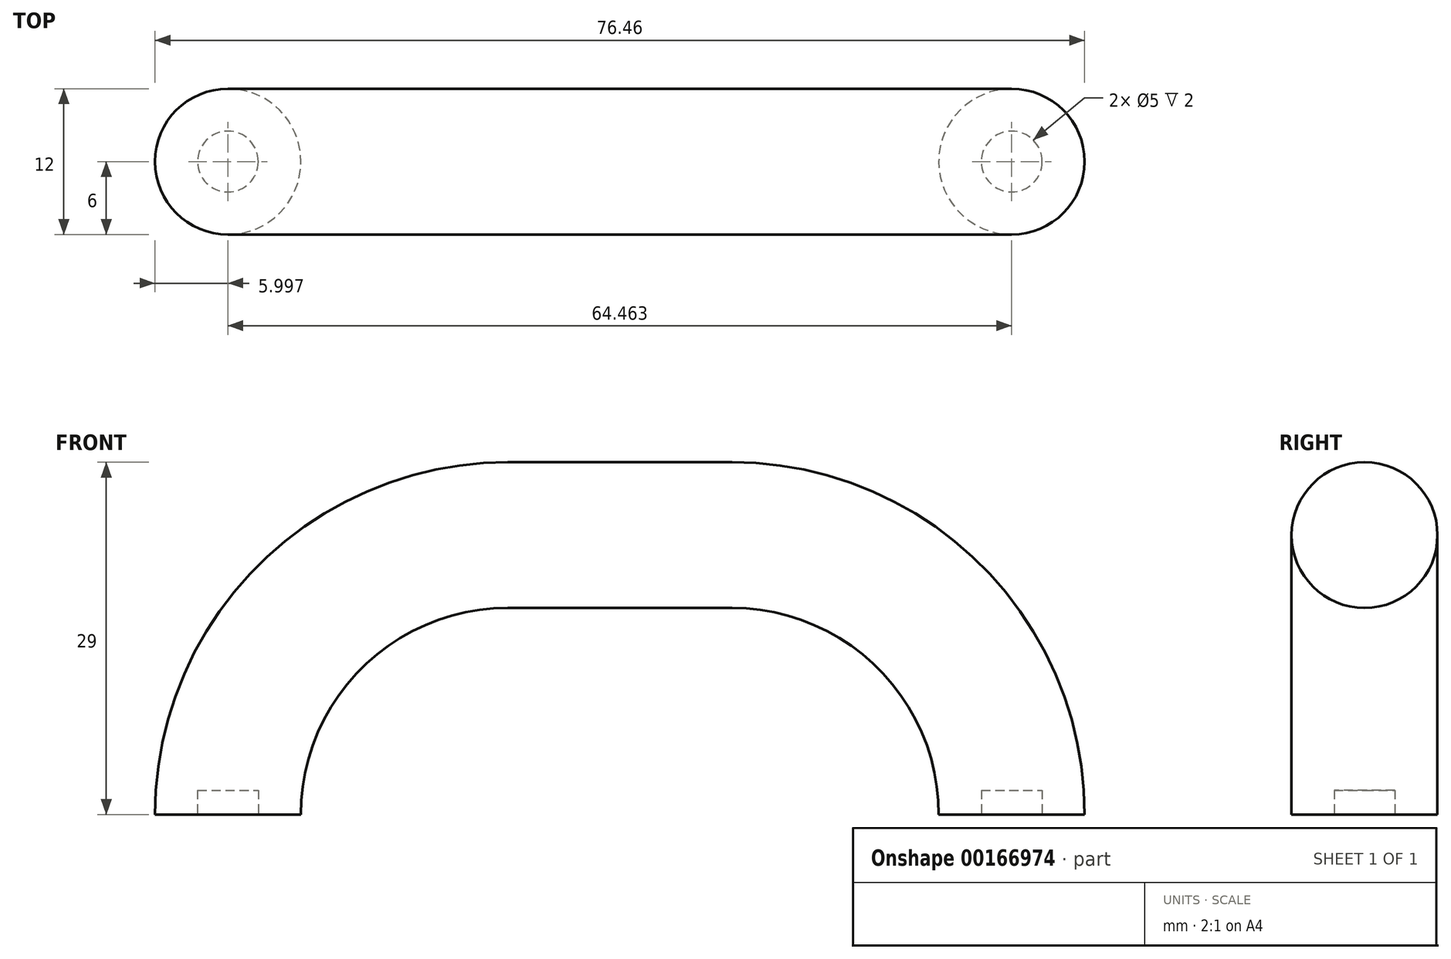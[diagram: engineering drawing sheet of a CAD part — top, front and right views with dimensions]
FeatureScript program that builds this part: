
annotation { "Feature Type Name" : "Feature", "Feature Type Description" : "" }
export const myFeature = defineFeature(function(context is Context, id is Id, definition is map)
    precondition{}
    {
        {
            var Q0;
            Q0=qCreatedBy(makeId("Top.planeOp"),FACE);
            var sketch = newSketch(context, id + "F0", { "sketchPlane" : qUnion([Q0])});
            skCircle(sketch, "E0", {"center": v(0, 0) * mm, "radius": 6 * mm});
            skSolve(sketch);
        }
        {
            var Q0;
            Q0=qCreatedBy(makeId("Front.planeOp"),FACE);
            var sketch = newSketch(context, id + "F1", { "sketchPlane" : qUnion([Q0])});
            skLineSegment(sketch, "E1.0", {"start": v(-6, 0) * mm, "end": v(6, 0) * mm});
            skLineSegment(sketch, "E2", {"start": v(6, 0) * mm, "end": v(6, 0) * mm});
            skLineSegment(sketch, "E3", {"start": v(-23, 29) * mm, "end": v(-32.23, 29) * mm});
            skPoint(sketch, "E4.start.orphan", {"position": v(-21.04, 0) * mm});
            skLineSegment(sketch, "E5", {"start": v(-32.23, 29) * mm, "end": v(-32.23, 0) * mm, "construction": true});
            skLineSegment(sketch, "E6.MirrorCS", {"start": v(-41.46, 29) * mm, "end": v(-32.23, 29) * mm});
            skLineSegment(sketch, "E7.MirrorCS", {"start": v(-58.46, 0) * mm, "end": v(-70.46, 0) * mm});
            skLineSegment(sketch, "E8.MirrorCS", {"start": v(-70.46, 0) * mm, "end": v(-70.46, 0) * mm});
            skPoint(sketch, "E9.visualSharp", {"position": v(6, 29) * mm});
            skArc(sketch, "E9.filletArc", {"start": v(6, 0) * mm, "mid": v(-2.5, 20.5) * mm, "end": v(-23, 29) * mm});
            skPoint(sketch, "E10.visualSharp", {"position": v(-70.46, 29) * mm});
            skArc(sketch, "E10.filletArc", {"start": v(-41.46, 29) * mm, "mid": v(-61.97, 20.5) * mm, "end": v(-70.46, 0) * mm});
            skSolve(sketch);
        }
        {
            var Q0;
            Q0=makeQuery(id+"F0.imprint","IMPRINT",FACE,{"disambiguationData":[TD([[makeQuery(id+"F0.imprint","IMPRINT",EDGE,{"derivedFrom":sQuery(id+"F0.wireOp",EDGE,"E0")}),1.0]])]});
            var Q1;
            Q1=sQuery(id+"F1.wireOp",EDGE,"E9.filletArc");
            var Q2;
            Q2=sQuery(id+"F1.wireOp",EDGE,"E3");
            var Q3;
            Q3=sQuery(id+"F1.wireOp",EDGE,"E6.MirrorCS");
            var Q4;
            Q4=sQuery(id+"F1.wireOp",EDGE,"E10.filletArc");
            sweep(context, id + "F2", {"profiles" : qUnion([Q0]), "path" : qUnion([Q1, Q2, Q3, Q4])});
        }
        {
            var Q0;
            Q0=makeQuery(id+"F2.opSweep","CAP_FACE",FACE,{"disambiguationData":[OSD([sQuery(id+"F0.wireOp",EDGE,"E0"),sQuery(id+"F1.wireOp",VERTEX,"E9.filletArc.start")])],"isStart":true});
            var sketch = newSketch(context, id + "F3", { "sketchPlane" : qUnion([Q0])});
            skCircle(sketch, "E11", {"center": v(0, 0) * mm, "radius": 2.5 * mm});
            skCircle(sketch, "E12", {"center": v(-64.46, 0) * mm, "radius": 2.5 * mm});
            skSolve(sketch);
        }
        {
            var Q0;
            Q0=makeQuery(id+"F3.imprint","IMPRINT",FACE,{"disambiguationData":[TD([[makeQuery(id+"F3.imprint","IMPRINT",EDGE,{"derivedFrom":sQuery(id+"F3.wireOp",EDGE,"E12")}),1.0]])]});
            extrude(context, id + "F4", {"entities" : qUnion([Q0]), "operationType" : NewBodyOperationType.REMOVE, "oppositeDirection" : true, "depth" : 2 * mm});
        }
        {
            var Q0;
            Q0=makeQuery(id+"F3.imprint","IMPRINT",FACE,{"disambiguationData":[TD([[makeQuery(id+"F3.imprint","IMPRINT",EDGE,{"derivedFrom":sQuery(id+"F3.wireOp",EDGE,"E11")}),1.0]])]});
            extrude(context, id + "F5", {"entities" : qUnion([Q0]), "operationType" : NewBodyOperationType.REMOVE, "oppositeDirection" : true, "depth" : 2 * mm});
        }
    });
